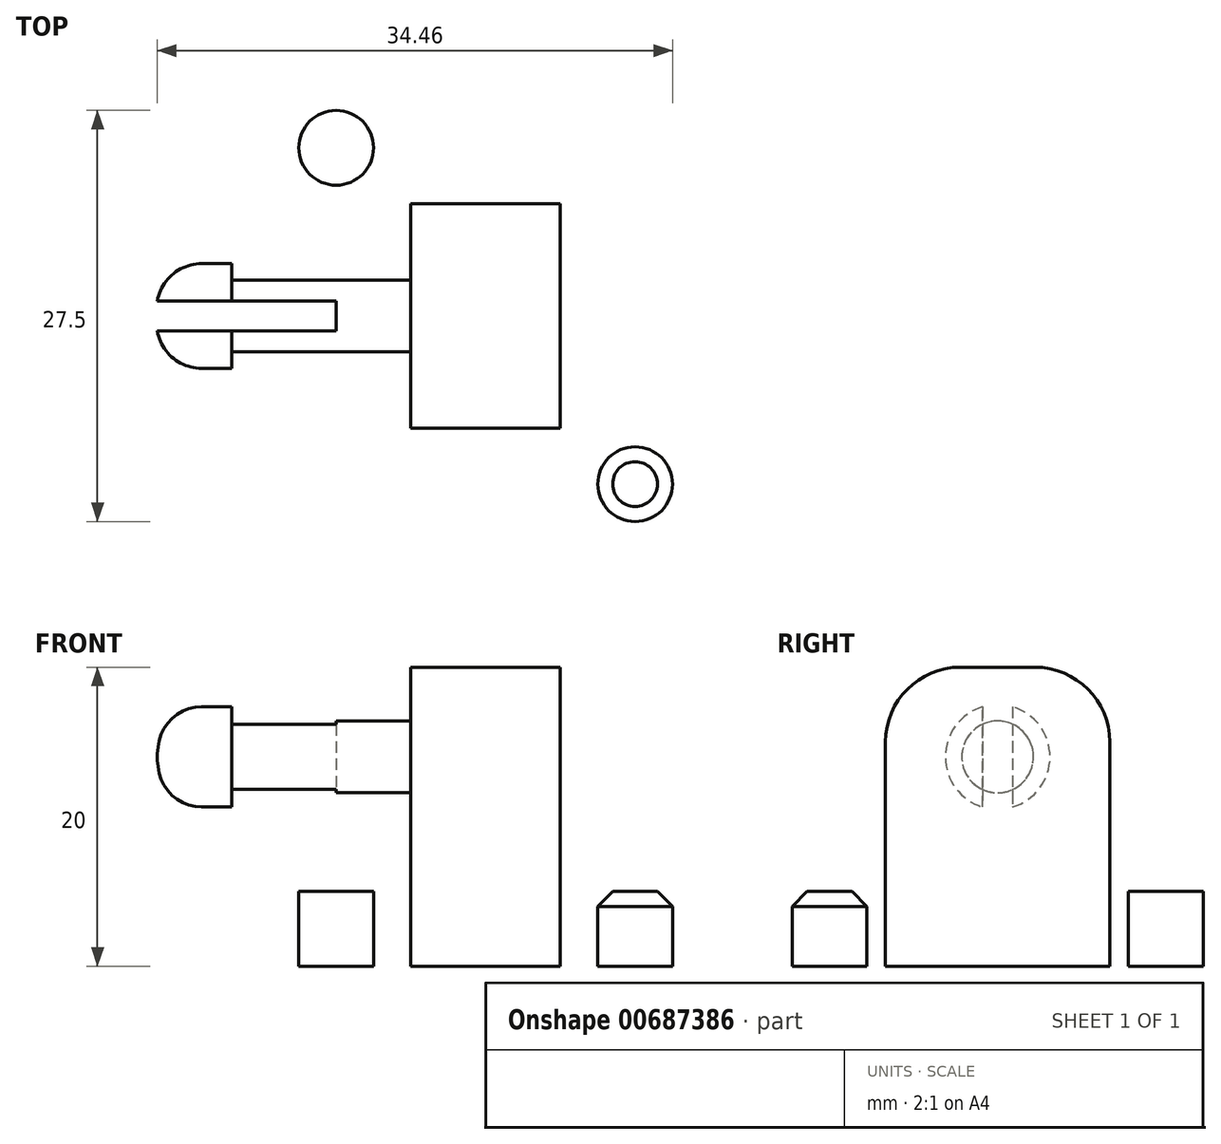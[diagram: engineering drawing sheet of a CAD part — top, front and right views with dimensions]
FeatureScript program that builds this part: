
annotation { "Feature Type Name" : "Feature", "Feature Type Description" : "" }
export const myFeature = defineFeature(function(context is Context, id is Id, definition is map)
    precondition{}
    {
        {
            var Q0;
            Q0=qCreatedBy(makeId("Top.planeOp"),FACE);
            var sketch = newSketch(context, id + "F0", { "sketchPlane" : qUnion([Q0])});
            skLineSegment(sketch, "E0.bottom", {"start": v(0, 0) * mm, "end": v(30, 0) * mm});
            skLineSegment(sketch, "E0.top", {"start": v(0, 30) * mm, "end": v(30, 30) * mm});
            skLineSegment(sketch, "E0.left", {"start": v(0, 0) * mm, "end": v(0, 30) * mm});
            skLineSegment(sketch, "E0.right", {"start": v(30, 0) * mm, "end": v(30, 30) * mm});
            skSolve(sketch);
        }
        {
            var Q0;
            Q0=makeQuery(id+"F0.imprint","IMPRINT",FACE,{"disambiguationData":[TD([[makeQuery(id+"F0.imprint","IMPRINT",EDGE,{"derivedFrom":sQuery(id+"F0.wireOp",EDGE,"E0.bottom")}),1.0]])]});
            extrude(context, id + "F1", {"entities" : qUnion([Q0]), "depth" : 5 * mm, "offsetDistance" : 25 * mm});
        }
        {
            var Q0;
            Q0=makeQuery(id+"F1.opExtrude","CAP_FACE",FACE,{"disambiguationData":[OSD([sQuery(id+"F0.wireOp",EDGE,"E0.bottom"),sQuery(id+"F0.wireOp",EDGE,"E0.top"),sQuery(id+"F0.wireOp",EDGE,"E0.left"),sQuery(id+"F0.wireOp",EDGE,"E0.right")])],"isStart":false});
            var sketch = newSketch(context, id + "F2", { "sketchPlane" : qUnion([Q0])});
            skLineSegment(sketch, "E1", {"start": v(15, 30) * mm, "end": v(15, 0) * mm, "construction": true});
            skLineSegment(sketch, "E2.top", {"start": v(15, 0) * mm, "end": v(0, 0) * mm});
            skLineSegment(sketch, "E2.left", {"start": v(15, 30) * mm, "end": v(15, 0) * mm});
            skLineSegment(sketch, "E3.bottom", {"start": v(20, 22.5) * mm, "end": v(10, 22.5) * mm});
            skLineSegment(sketch, "E3.top", {"start": v(20, 7.5) * mm, "end": v(10, 7.5) * mm});
            skLineSegment(sketch, "E3.left", {"start": v(20, 22.5) * mm, "end": v(20, 7.5) * mm});
            skLineSegment(sketch, "E3.right", {"start": v(10, 22.5) * mm, "end": v(10, 7.5) * mm});
            skPoint(sketch, "E3.middle", {"position": v(15, 15) * mm});
            skSolve(sketch);
        }
        {
            var Q0;
            {var subQ5=sQuery(id+"F2.wireOp",EDGE,"E3.left");Q0=makeQuery(id+"F2.imprint","IMPRINT",FACE,{"disambiguationData":[TD([[makeQuery(id+"F2.imprint","IMPRINT",EDGE,{"derivedFrom":subQ5}),-1.0]])]});}
            var Q1;
            {var subQ5=sQuery(id+"F2.wireOp",EDGE,"E3.right");Q1=makeQuery(id+"F2.imprint","IMPRINT",FACE,{"disambiguationData":[TD([[makeQuery(id+"F2.imprint","IMPRINT",EDGE,{"derivedFrom":subQ5}),1.0]])]});}
            extrude(context, id + "F3", {"entities" : qUnion([Q0, Q1]), "operationType" : NewBodyOperationType.ADD, "depth" : 15 * mm, "offsetDistance" : 25 * mm});
        }
        {
            var Q0;
            Q0=makeQuery(id+"F3.opExtrude","SWEPT_FACE",FACE,{"disambiguationData":[OSD([sQuery(id+"F2.wireOp",EDGE,"E3.right")])]});
            var sketch = newSketch(context, id + "F4", { "sketchPlane" : qUnion([Q0])});
            skCircle(sketch, "E4", {"center": v(-15, 14) * mm, "radius": 2.4 * mm});
            skPoint(sketch, "E4.centerSnap0", {"position": v(-15, 20) * mm});
            skSolve(sketch);
        }
        {
            var Q0;
            Q0=makeQuery(id+"F4.imprint","IMPRINT",FACE,{"disambiguationData":[TD([[makeQuery(id+"F4.imprint","IMPRINT",EDGE,{"derivedFrom":sQuery(id+"F4.wireOp",EDGE,"E4")}),1.0]])]});
            extrude(context, id + "F5", {"entities" : qUnion([Q0]), "operationType" : NewBodyOperationType.ADD, "depth" : 12 * mm, "offsetDistance" : 25 * mm});
        }
        {
            var Q0;
            Q0=makeQuery(id+"F1.opExtrude","CAP_FACE",FACE,{"disambiguationData":[OSD([sQuery(id+"F0.wireOp",EDGE,"E0.bottom"),sQuery(id+"F0.wireOp",EDGE,"E0.top"),sQuery(id+"F0.wireOp",EDGE,"E0.left"),sQuery(id+"F0.wireOp",EDGE,"E0.right")])],"isStart":false});
            var sketch = newSketch(context, id + "F6", { "sketchPlane" : qUnion([Q0])});
            skLineSegment(sketch, "E5", {"start": v(20, 22.5) * mm, "end": v(30, 30) * mm, "construction": true});
            skCircle(sketch, "E6", {"center": v(25, 26.25) * mm, "radius": 2.5 * mm});
            skLineSegment(sketch, "E7", {"start": v(15, 30) * mm, "end": v(15, 0) * mm, "construction": true});
            skLineSegment(sketch, "E8", {"start": v(30, 15) * mm, "end": v(0, 15) * mm, "construction": true});
            skCircle(sketch, "E9.MirrorC", {"center": v(5, 26.25) * mm, "radius": 2.5 * mm});
            skLineSegment(sketch, "E10.MirrorCS", {"start": v(0, 15) * mm, "end": v(30, 15) * mm, "construction": true});
            skCircle(sketch, "E11.MirrorC", {"center": v(5, 3.75) * mm, "radius": 2.5 * mm});
            skCircle(sketch, "E12.MirrorC", {"center": v(25, 3.75) * mm, "radius": 2.5 * mm});
            skSolve(sketch);
        }
        {
            var Q0;
            Q0=makeQuery(id+"F6.imprint","IMPRINT",FACE,{"disambiguationData":[TD([[makeQuery(id+"F6.imprint","IMPRINT",EDGE,{"derivedFrom":sQuery(id+"F6.wireOp",EDGE,"E6")}),1.0]])]});
            var Q1;
            Q1=makeQuery(id+"F6.imprint","IMPRINT",FACE,{"disambiguationData":[TD([[makeQuery(id+"F6.imprint","IMPRINT",EDGE,{"derivedFrom":sQuery(id+"F6.wireOp",EDGE,"E9.MirrorC")}),-1.0]])]});
            var Q2;
            Q2=makeQuery(id+"F6.imprint","IMPRINT",FACE,{"disambiguationData":[TD([[makeQuery(id+"F6.imprint","IMPRINT",EDGE,{"derivedFrom":sQuery(id+"F6.wireOp",EDGE,"E11.MirrorC")}),1.0]])]});
            var Q3;
            Q3=makeQuery(id+"F6.imprint","IMPRINT",FACE,{"disambiguationData":[TD([[makeQuery(id+"F6.imprint","IMPRINT",EDGE,{"derivedFrom":sQuery(id+"F6.wireOp",EDGE,"E12.MirrorC")}),-1.0]])]});
            extrude(context, id + "F7", {"entities" : qUnion([Q0, Q1, Q2, Q3]), "operationType" : NewBodyOperationType.REMOVE, "endBound" : BoundingType.UP_TO_NEXT, "oppositeDirection" : true, "depth" : 25 * mm, "offsetDistance" : 25 * mm});
        }
        {
            var Q0;
            Q0=makeQuery(id+"F7.boolean.opBoolean","COPY",EDGE,{"derivedFrom":makeQuery(id+"F7.opExtrude","CAP_EDGE",EDGE,{"disambiguationData":[OSD([sQuery(id+"F6.wireOp",EDGE,"E9.MirrorC")])],"isStart":true})});
            var Q1;
            Q1=makeQuery(id+"F7.boolean.opBoolean","COPY",EDGE,{"derivedFrom":makeQuery(id+"F7.opExtrude","CAP_EDGE",EDGE,{"disambiguationData":[OSD([sQuery(id+"F6.wireOp",EDGE,"E6")])],"isStart":true})});
            var Q2;
            Q2=makeQuery(id+"F7.boolean.opBoolean","COPY",EDGE,{"derivedFrom":makeQuery(id+"F7.opExtrude","CAP_EDGE",EDGE,{"disambiguationData":[OSD([sQuery(id+"F6.wireOp",EDGE,"E12.MirrorC")])],"isStart":true})});
            var Q3;
            Q3=makeQuery(id+"F7.boolean.opBoolean","COPY",EDGE,{"derivedFrom":makeQuery(id+"F7.opExtrude","CAP_EDGE",EDGE,{"disambiguationData":[OSD([sQuery(id+"F6.wireOp",EDGE,"E11.MirrorC")])],"isStart":true})});
            chamfer(context, id + "F8", {"entities" : qUnion([Q0, Q1, Q2, Q3]), "width" : 1 * mm, "tangentPropagation" : true});
        }
        {
            var Q0;
            Q0=makeQuery(id+"F3.opExtrude","CAP_EDGE",EDGE,{"disambiguationData":[OSD([sQuery(id+"F2.wireOp",EDGE,"E3.bottom")])],"isStart":false});
            var Q1;
            Q1=makeQuery(id+"F3.opExtrude","CAP_EDGE",EDGE,{"disambiguationData":[OSD([sQuery(id+"F2.wireOp",EDGE,"E3.top")])],"isStart":false});
            fillet(context, id + "F9", {"entities" : qUnion([Q0, Q1]), "radius" : 5 * mm, "tangentPropagation" : true, "allowEdgeOverflow" : false});
        }
        {
            var Q0;
            Q0=makeQuery(id+"F5.opExtrude","CAP_FACE",FACE,{"disambiguationData":[OSD([sQuery(id+"F4.wireOp",EDGE,"E4")])],"isStart":false});
            var sketch = newSketch(context, id + "F10", { "sketchPlane" : qUnion([Q0])});
            skCircle(sketch, "E13", {"center": v(-15, 14) * mm, "radius": 3.5 * mm});
            skLineSegment(sketch, "E14.bottom", {"start": v(-16, 17.85) * mm, "end": v(-14, 17.85) * mm});
            skLineSegment(sketch, "E14.top", {"start": v(-16, 10.15) * mm, "end": v(-14, 10.15) * mm});
            skLineSegment(sketch, "E14.left", {"start": v(-16, 17.85) * mm, "end": v(-16, 10.15) * mm});
            skLineSegment(sketch, "E14.right", {"start": v(-14, 17.85) * mm, "end": v(-14, 10.15) * mm});
            skSolve(sketch);
        }
        {
            var Q0;
            {var subQ0=sQuery(id+"F10.wireOp",EDGE,"E14.left");var subQ1=sQuery(id+"F10.wireOp",EDGE,"E13");var subQ2=makeQuery(id+"F10.imprint","INTERSECT",VERTEX,{"disambiguationData":[OD(0.0)],"derivedFrom":[subQ1,subQ0]});Q0=makeQuery(id+"F10.imprint","IMPRINT",FACE,{"disambiguationData":[TD([[makeQuery(id+"F10.imprint","IMPRINT",EDGE,{"disambiguationData":[TD([[subQ2,-1.0]])],"derivedFrom":subQ1}),1.0]])]});}
            var Q1;
            {var subQ0=sQuery(id+"F10.wireOp",EDGE,"E14.right");var subQ1=sQuery(id+"F10.wireOp",EDGE,"E13");var subQ2=makeQuery(id+"F10.imprint","INTERSECT",VERTEX,{"disambiguationData":[OD(0.0)],"derivedFrom":[subQ1,subQ0]});Q1=makeQuery(id+"F10.imprint","IMPRINT",FACE,{"disambiguationData":[TD([[makeQuery(id+"F10.imprint","IMPRINT",EDGE,{"disambiguationData":[TD([[subQ2,1.0]])],"derivedFrom":subQ1}),1.0]])]});}
            var Q2;
            {var subQ0=sQuery(id+"F10.wireOp",EDGE,"E14.right");var subQ1=makeQuery(id+"F5.opExtrude","CAP_EDGE",EDGE,{"disambiguationData":[OSD([sQuery(id+"F4.wireOp",EDGE,"E4")])],"isStart":false});var subQ2=makeQuery(id+"F10.imprint","INTERSECT",VERTEX,{"disambiguationData":[OD(0.0)],"derivedFrom":[subQ1,subQ0]});Q2=makeQuery(id+"F10.imprint","IMPRINT",FACE,{"disambiguationData":[TD([[makeQuery(id+"F10.imprint","IMPRINT",EDGE,{"disambiguationData":[TD([[subQ2,-1.0]])],"derivedFrom":subQ0}),1.0]])]});}
            var Q3;
            {var subQ0=sQuery(id+"F10.wireOp",EDGE,"E14.left");var subQ1=makeQuery(id+"F5.opExtrude","CAP_EDGE",EDGE,{"disambiguationData":[OSD([sQuery(id+"F4.wireOp",EDGE,"E4")])],"isStart":false});var subQ2=makeQuery(id+"F10.imprint","INTERSECT",VERTEX,{"disambiguationData":[OD(0.0)],"derivedFrom":[subQ1,subQ0]});Q3=makeQuery(id+"F10.imprint","IMPRINT",FACE,{"disambiguationData":[TD([[makeQuery(id+"F10.imprint","IMPRINT",EDGE,{"disambiguationData":[TD([[subQ2,-1.0]])],"derivedFrom":subQ0}),-1.0]])]});}
            extrude(context, id + "F11", {"entities" : qUnion([Q0, Q1, Q2, Q3]), "operationType" : NewBodyOperationType.ADD, "depth" : 5 * mm, "offsetDistance" : 25 * mm});
        }
        {
            var Q0;
            {var subQ0=sQuery(id+"F10.wireOp",EDGE,"E14.left");var subQ1=sQuery(id+"F10.wireOp",EDGE,"E13");Q0=makeQuery(id+"F11.opExtrude","CAP_EDGE",EDGE,{"disambiguationData":[OSD([subQ1]),TDD([makeQuery(id+"F10.imprint","IMPRINT",EDGE,{"disambiguationData":[TD([[makeQuery(id+"F10.imprint","INTERSECT",VERTEX,{"disambiguationData":[OD(0.0)],"derivedFrom":[subQ1,subQ0]}),-1.0]])],"derivedFrom":subQ1})])],"isStart":false});}
            var Q1;
            {var subQ0=sQuery(id+"F10.wireOp",EDGE,"E14.right");var subQ1=sQuery(id+"F10.wireOp",EDGE,"E13");Q1=makeQuery(id+"F11.opExtrude","CAP_EDGE",EDGE,{"disambiguationData":[OSD([subQ1]),TDD([makeQuery(id+"F10.imprint","IMPRINT",EDGE,{"disambiguationData":[TD([[makeQuery(id+"F10.imprint","INTERSECT",VERTEX,{"disambiguationData":[OD(0.0)],"derivedFrom":[subQ1,subQ0]}),1.0]])],"derivedFrom":subQ1})])],"isStart":false});}
            fillet(context, id + "F12", {"entities" : qUnion([Q0, Q1]), "radius" : 3 * mm, "tangentPropagation" : true, "allowEdgeOverflow" : false});
        }
        {
            var Q0;
            Q0=makeQuery(id+"F5.opExtrude","CAP_FACE",FACE,{"disambiguationData":[OSD([sQuery(id+"F4.wireOp",EDGE,"E4")])],"isStart":false});
            extrude(context, id + "F13", {"entities" : qUnion([Q0]), "operationType" : NewBodyOperationType.REMOVE, "oppositeDirection" : true, "depth" : 7 * mm, "offsetDistance" : 25 * mm});
        }
    });
